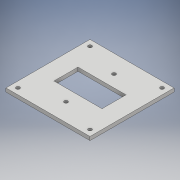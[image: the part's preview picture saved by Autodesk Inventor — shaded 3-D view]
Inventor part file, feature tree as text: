
AUTODESK INVENTOR PART (.ipt)
format: ipt  version: 2017 (Build 210142000, 142)  size: 124,416 bytes
history: native  units: mm
features: extrude x1, sketch x1
ambient origin geometry x8: Origin, YZ Plane, XZ Plane, XY Plane, X Axis, Y Axis, Z Axis, Center Point
bodies: Body1 (feature_tree)
feature tree (2):
  extrude  "Extrusion3"  Depth=20.0mm
  sketch  "Sketch1"  dims[d0=40.0mm d1=20.0mm d2=10.0mm d3=70.0mm d4=70.0mm d9=3.0mm d10=3.0mm d11=3.0mm d12=3.0mm d15=10.0mm d16=10.0mm d17=3.0mm d18=3.0mm d19=3.0mm d20=0.0mm]
